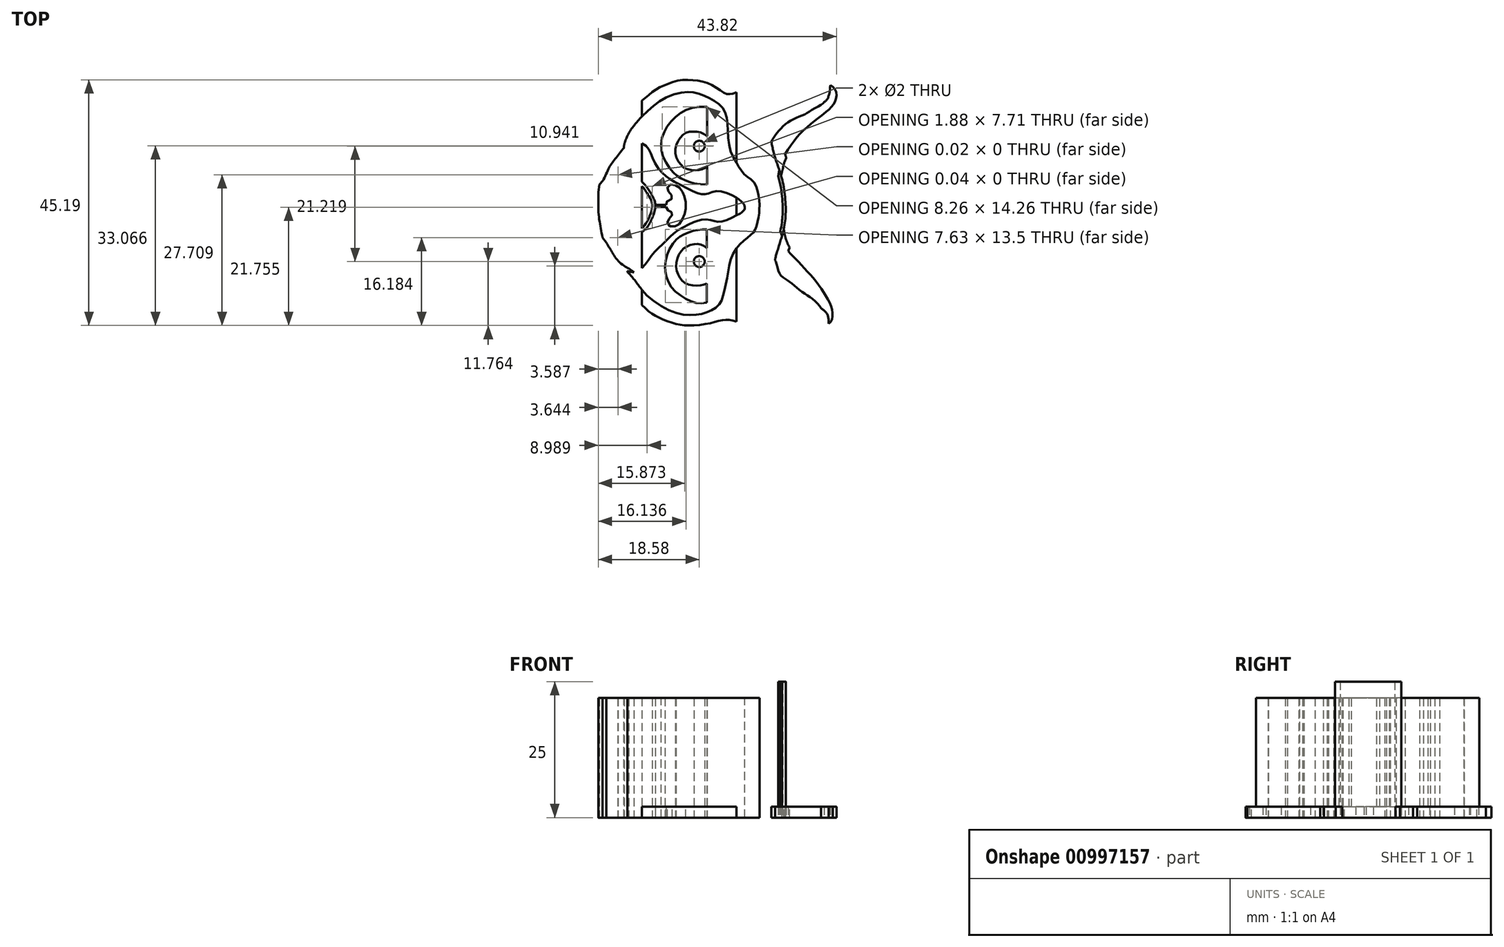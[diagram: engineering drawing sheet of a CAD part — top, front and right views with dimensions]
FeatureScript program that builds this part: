
annotation { "Feature Type Name" : "Feature", "Feature Type Description" : "" }
export const myFeature = defineFeature(function(context is Context, id is Id, definition is map)
    precondition{}
    {
        {
            var Q0;
            Q0=qCreatedBy(makeId("Top.planeOp"),FACE);
            var sketch = newSketch(context, id + "F0", { "sketchPlane" : qUnion([Q0])});
            skLineSegment(sketch, "E0", {"start": v(52.2, -25.32) * mm, "end": v(52.2, -39.58) * mm});
            skLineSegment(sketch, "E1", {"start": v(52.14, -47.83) * mm, "end": v(52.14, -61.33) * mm});
            skFitSpline(sketch, "E2", {"points": [v(52.2, -25.32) * mm, v(47.39, -26.41) * mm, v(44.48, -29.6) * mm, v(43.86, -33.55) * mm, v(45.93, -37.28) * mm, v(48, -38.74) * mm, v(50.09, -39.43) * mm, v(52.2, -39.58) * mm], "startDerivative": vector(-35.94, 2.58) * mm, "endDerivative": vector(39.25, -3.06) * mm});
            skFitSpline(sketch, "E3", {"points": [v(52.14, -61.33) * mm, v(50.12, -61.33) * mm, v(48.02, -60.44) * mm, v(45.82, -58.67) * mm, v(44.71, -56.52) * mm, v(44.48, -54.66) * mm, v(44.96, -52.24) * mm, v(46.4, -49.9) * mm, v(47.49, -49.02) * mm, v(49.12, -48.26) * mm, v(50.68, -47.93) * mm, v(52.14, -47.83) * mm], "startDerivative": vector(-24.82, -2.43) * mm, "endDerivative": vector(19.62, -0.27) * mm});
            skFitSpline(sketch, "E4", {"points": [v(52.14, -51.25) * mm, v(51.1, -50.64) * mm, v(49.91, -50.52) * mm, v(48.55, -50.96) * mm, v(47.44, -51.83) * mm, v(46.65, -53.43) * mm, v(46.57, -55.15) * mm, v(47.12, -56.58) * mm, v(48.17, -57.68) * mm, v(49.56, -58.15) * mm, v(51.14, -58.12) * mm, v(52.14, -57.83) * mm], "startDerivative": vector(-12, 8.58) * mm, "endDerivative": vector(12.04, 4.34) * mm});
            skFitSpline(sketch, "E5", {"points": [v(52.2, -30.7) * mm, v(51.23, -30.07) * mm, v(49.95, -29.86) * mm, v(48.84, -29.9) * mm, v(47.8, -30.42) * mm, v(46.94, -31.46) * mm, v(46.45, -32.77) * mm, v(46.45, -34.43) * mm, v(47.32, -35.85) * mm, v(48.18, -36.61) * mm, v(49.57, -36.96) * mm, v(50.74, -36.89) * mm, v(51.64, -36.61) * mm, v(52.2, -36.16) * mm], "startDerivative": vector(-12.11, 9.76) * mm, "endDerivative": vector(8.55, 8.45) * mm});
            skCircle(sketch, "E6", {"center": v(50.77, -53.76) * mm, "radius": 1 * mm});
            skCircle(sketch, "E7", {"center": v(50.77, -32.54) * mm, "radius": 1 * mm});
            skFitSpline(sketch, "E8", {"points": [v(35.01, -37.86) * mm, v(37.23, -37.99) * mm, v(39.56, -39.23) * mm, v(41.03, -40.95) * mm, v(41.77, -42.17) * mm, v(42.12, -43.51) * mm, v(41.57, -45.55) * mm, v(40.54, -47.31) * mm, v(39.33, -48.26) * mm, v(37.21, -49.17) * mm, v(34.82, -49.32) * mm], "startDerivative": vector(20.16, 2.55) * mm, "endDerivative": vector(-22.5, 0.89) * mm});
            skFitSpline(sketch, "E9.0", {"points": [v(34.94, -37.3) * mm, v(35.4, -37.25) * mm, v(36.1, -37.22) * mm, v(37.1, -37.36) * mm, v(37.86, -37.58) * mm, v(38.59, -37.9) * mm, v(39.28, -38.3) * mm, v(39.92, -38.78) * mm, v(40.48, -39.32) * mm, v(40.95, -39.88) * mm, v(41.35, -40.42) * mm, v(41.7, -40.92) * mm, v(41.99, -41.39) * mm, v(42.2, -41.78) * mm, v(42.36, -42.12) * mm, v(42.51, -42.48) * mm, v(42.63, -42.88) * mm, v(42.68, -43.32) * mm, v(42.68, -43.8) * mm, v(42.59, -44.38) * mm, v(42.37, -45.07) * mm, v(42.1, -45.74) * mm, v(41.8, -46.39) * mm, v(41.47, -47) * mm, v(41.16, -47.46) * mm, v(40.87, -47.8) * mm, v(40.57, -48.09) * mm, v(40.25, -48.34) * mm, v(39.92, -48.56) * mm, v(39.65, -48.72) * mm, v(39.38, -48.88) * mm, v(38.98, -49.1) * mm, v(38.43, -49.36) * mm, v(37.72, -49.63) * mm, v(36.97, -49.81) * mm, v(36.23, -49.89) * mm, v(35.5, -49.9) * mm, v(35.03, -49.89) * mm, v(34.8, -49.88) * mm]});
            skLineSegment(sketch, "E10", {"start": v(44.65, -43.32) * mm, "end": v(42.67, -43.32) * mm});
            skLineSegment(sketch, "E11", {"start": v(44.66, -43.71) * mm, "end": v(42.67, -43.71) * mm});
            skPoint(sketch, "E12.orphan", {"position": v(44.65, -43.51) * mm});
            skFitSpline(sketch, "E13.trimOffspring", {"points": [v(34.94, -37.3) * mm, v(35.4, -37.25) * mm, v(36.1, -37.22) * mm, v(37.1, -37.36) * mm, v(37.86, -37.58) * mm, v(38.59, -37.9) * mm, v(39.28, -38.3) * mm, v(39.92, -38.78) * mm, v(40.48, -39.32) * mm, v(40.95, -39.88) * mm, v(41.35, -40.42) * mm, v(41.7, -40.92) * mm, v(41.99, -41.39) * mm, v(42.2, -41.78) * mm, v(42.36, -42.12) * mm, v(42.51, -42.48) * mm, v(42.63, -42.88) * mm, v(42.68, -43.32) * mm, v(42.68, -43.8) * mm, v(42.59, -44.38) * mm, v(42.37, -45.07) * mm, v(42.1, -45.74) * mm, v(41.8, -46.39) * mm, v(41.47, -47) * mm, v(41.16, -47.46) * mm, v(40.87, -47.8) * mm, v(40.57, -48.09) * mm, v(40.25, -48.34) * mm, v(39.92, -48.56) * mm, v(39.65, -48.72) * mm, v(39.38, -48.88) * mm, v(38.98, -49.1) * mm, v(38.43, -49.36) * mm, v(37.72, -49.63) * mm, v(36.97, -49.81) * mm, v(36.23, -49.89) * mm, v(35.5, -49.9) * mm, v(35.03, -49.89) * mm, v(34.8, -49.88) * mm]});
            skPoint(sketch, "E14.third.point", {"position": v(34.82, -37.86) * mm});
            skArc(sketch, "E15", {"start": v(34.77, -49.88) * mm, "mid": v(34.78, -49.88) * mm, "end": v(34.8, -49.88) * mm});
            skPoint(sketch, "E15.third.point", {"position": v(34.77, -49.88) * mm});
            skFitSpline(sketch, "E16", {"points": [v(44.66, -43.71) * mm, v(44.87, -44.24) * mm, v(45.29, -44.53) * mm, v(45.7, -44.7) * mm, v(45.82, -45) * mm, v(45.57, -45.5) * mm, v(45.12, -46) * mm, v(44.92, -46.48) * mm, v(45.12, -47.1) * mm, v(45.82, -47.32) * mm, v(46.63, -47.2) * mm, v(47.22, -46.71) * mm, v(47.77, -45.74) * mm, v(48.18, -44.68) * mm, v(48.29, -43.71) * mm, v(48.18, -42.21) * mm, v(47.95, -41.54) * mm, v(47.59, -40.82) * mm, v(47.03, -40.07) * mm, v(46.38, -39.69) * mm, v(45.59, -39.58) * mm, v(45, -39.89) * mm, v(44.92, -40.48) * mm, v(45.2, -40.95) * mm, v(45.66, -41.56) * mm, v(45.78, -42.16) * mm, v(45.14, -42.44) * mm, v(44.66, -42.96) * mm, v(44.65, -43.32) * mm], "startDerivative": vector(-1.35, -20.13) * mm, "endDerivative": vector(4.82, -19.1) * mm});
            skFitSpline(sketch, "E17", {"points": [v(61.85, -43.78) * mm, v(61.66, -45.64) * mm, v(61.1, -47.77) * mm, v(60.36, -48.77) * mm, v(58.46, -50.33) * mm, v(56.64, -53.16) * mm, v(55.93, -56.55) * mm, v(55.22, -59.79) * mm, v(54.44, -61.65) * mm, v(52.73, -62.88) * mm, v(50.2, -63.55) * mm, v(46.29, -63.14) * mm, v(40.9, -59.71) * mm, v(38.44, -56.62) * mm, v(37.55, -55.56) * mm, v(39.03, -55.7) * mm, v(40.9, -54.17) * mm, v(42.5, -52.08) * mm, v(44.65, -49.92) * mm, v(46.66, -48.14) * mm, v(49.64, -46.57) * mm, v(51.43, -46.02) * mm, v(53.4, -46.24) * mm, v(54.63, -46.46) * mm, v(57.2, -45.46) * mm, v(58.6, -44.68) * mm, v(59.13, -44.04) * mm, v(59.13, -43.6) * mm, v(58.83, -43) * mm, v(57.83, -42.15) * mm, v(56.49, -41.44) * mm, v(54.51, -40.8) * mm, v(53.17, -41) * mm, v(52.36, -41.29) * mm, v(51.57, -41.36) * mm, v(50.57, -41.21) * mm, v(48.9, -40.47) * mm, v(46.1, -39.02) * mm, v(44.8, -38.16) * mm, v(43.54, -37) * mm, v(42.3, -34.96) * mm, v(41.71, -33.55) * mm, v(41.04, -32.54) * mm, v(39.7, -31.8) * mm, v(38.06, -31.8) * mm, v(36.95, -32.8) * mm, v(37.17, -31.58) * mm, v(38.66, -28.86) * mm, v(41.53, -25.84) * mm, v(44.43, -23.69) * mm, v(48.11, -22.57) * mm, v(50.23, -22.76) * mm, v(52.24, -23.5) * mm, v(53.92, -24.47) * mm, v(55.26, -25.77) * mm, v(55.85, -27.6) * mm, v(56.08, -30.53) * mm, v(56.56, -33.59) * mm, v(57.72, -35.74) * mm, v(59.06, -37.72) * mm, v(60.73, -39.06) * mm, v(61.62, -41.25) * mm, v(61.85, -43.78) * mm]});
            skFitSpline(sketch, "E18", {"points": [v(64.7, -53.55) * mm, v(65.46, -55.81) * mm, v(66.99, -57.18) * mm, v(69.43, -59.13) * mm, v(72.07, -61.03) * mm, v(73.3, -62.63) * mm, v(72.88, -62.6) * mm, v(69.9, -62.87) * mm, v(66.9, -62.97) * mm, v(64.85, -61.66) * mm, v(63.46, -59.2) * mm, v(63.04, -56.95) * mm, v(63.64, -55.13) * mm, v(64.7, -53.55) * mm]});
            skFitSpline(sketch, "E19", {"points": [v(64.02, -31.7) * mm, v(64.56, -34.1) * mm, v(65.35, -36.47) * mm, v(66.19, -39.41) * mm, v(66.66, -43.47) * mm, v(66.5, -46.78) * mm, v(65.82, -49.6) * mm, v(64.77, -53.12) * mm, v(64.7, -53.55) * mm], "startDerivative": vector(3.95, -20.11) * mm, "endDerivative": vector(-0.5, -6.13) * mm});
            skFitSpline(sketch, "E20.0", {"points": [v(63.47, -31.8) * mm, v(63.55, -32.22) * mm, v(63.68, -32.86) * mm, v(63.87, -33.7) * mm, v(64.04, -34.34) * mm, v(64.23, -34.97) * mm, v(64.51, -35.78) * mm, v(64.88, -36.8) * mm, v(65.3, -38.08) * mm, v(65.65, -39.47) * mm, v(65.91, -41.04) * mm, v(66.05, -42.4) * mm, v(66.1, -43.48) * mm, v(66.12, -44.26) * mm, v(66.1, -45) * mm, v(66.06, -45.72) * mm, v(66, -46.4) * mm, v(65.87, -47.23) * mm, v(65.7, -48.02) * mm, v(65.47, -48.8) * mm, v(65.32, -49.3) * mm, v(65.16, -49.83) * mm, v(64.94, -50.55) * mm, v(64.68, -51.41) * mm, v(64.44, -52.2) * mm, v(64.29, -52.73) * mm, v(64.2, -53.05) * mm, v(64.16, -53.3) * mm, v(64.15, -53.44) * mm, v(64.14, -53.5) * mm]});
            skFitSpline(sketch, "E20.1", {"points": [v(63.47, -31.8) * mm, v(63.55, -32.22) * mm, v(63.68, -32.86) * mm, v(63.87, -33.7) * mm, v(64.04, -34.34) * mm, v(64.23, -34.97) * mm, v(64.51, -35.78) * mm, v(64.88, -36.8) * mm, v(65.3, -38.08) * mm, v(65.65, -39.47) * mm, v(65.91, -41.04) * mm, v(66.05, -42.4) * mm, v(66.1, -43.48) * mm, v(66.12, -44.26) * mm, v(66.1, -45) * mm, v(66.06, -45.72) * mm, v(66, -46.4) * mm, v(65.87, -47.23) * mm, v(65.7, -48.02) * mm, v(65.47, -48.8) * mm, v(65.32, -49.3) * mm, v(65.16, -49.83) * mm, v(64.94, -50.55) * mm, v(64.68, -51.41) * mm, v(64.44, -52.2) * mm, v(64.29, -52.73) * mm, v(64.2, -53.05) * mm, v(64.16, -53.3) * mm, v(64.15, -53.44) * mm, v(64.14, -53.5) * mm]});
            skFitSpline(sketch, "E20.2", {"points": [v(63.47, -31.8) * mm, v(63.55, -32.22) * mm, v(63.68, -32.86) * mm, v(63.87, -33.7) * mm, v(64.04, -34.34) * mm, v(64.23, -34.97) * mm, v(64.51, -35.78) * mm, v(64.88, -36.8) * mm, v(65.3, -38.08) * mm, v(65.65, -39.47) * mm, v(65.91, -41.04) * mm, v(66.05, -42.4) * mm, v(66.1, -43.48) * mm, v(66.12, -44.26) * mm, v(66.1, -45) * mm, v(66.06, -45.72) * mm, v(66, -46.4) * mm, v(65.87, -47.23) * mm, v(65.7, -48.02) * mm, v(65.47, -48.8) * mm, v(65.32, -49.3) * mm, v(65.16, -49.83) * mm, v(64.94, -50.55) * mm, v(64.68, -51.41) * mm, v(64.44, -52.2) * mm, v(64.29, -52.73) * mm, v(64.2, -53.05) * mm, v(64.16, -53.3) * mm, v(64.15, -53.44) * mm, v(64.14, -53.5) * mm]});
            skLineSegment(sketch, "E21", {"start": v(64.14, -53.47) * mm, "end": v(64.06, -54.29) * mm});
            skLineSegment(sketch, "E22", {"start": v(65.48, -36.87) * mm, "end": v(65.28, -38.1) * mm});
            skLineSegment(sketch, "E23", {"start": v(65.98, -49.06) * mm, "end": v(65.66, -48.12) * mm});
            skFitSpline(sketch, "E24", {"points": [v(36.95, -32.8) * mm, v(35.31, -34.84) * mm, v(34.2, -36.44) * mm, v(33.01, -38.91) * mm], "startDerivative": vector(-5.17, -6.03) * mm, "endDerivative": vector(-3.98, -7.08) * mm});
            skFitSpline(sketch, "E25", {"points": [v(37.55, -55.56) * mm, v(35.43, -53.97) * mm, v(34.08, -52.05) * mm, v(33.19, -50.54) * mm], "startDerivative": vector(-6.96, 3.5) * mm, "endDerivative": vector(-3.36, 5.63) * mm});
            skFitSpline(sketch, "E26.0", {"points": [v(36.52, -32.44) * mm, v(36.3, -32.7) * mm, v(35.88, -33.21) * mm, v(35.38, -33.84) * mm, v(35.01, -34.32) * mm, v(34.66, -34.76) * mm, v(34.25, -35.3) * mm, v(33.86, -35.9) * mm, v(33.56, -36.45) * mm, v(33.3, -37.03) * mm, v(32.96, -37.78) * mm, v(32.68, -38.36) * mm, v(32.52, -38.64) * mm]});
            skLineSegment(sketch, "E27", {"start": v(36.5, -32.46) * mm, "end": v(37.1, -31.79) * mm});
            skFitSpline(sketch, "E28.0", {"points": [v(37.8, -55.06) * mm, v(37.53, -54.92) * mm, v(37.03, -54.63) * mm, v(36.36, -54.13) * mm, v(35.78, -53.55) * mm, v(35.27, -52.89) * mm, v(34.88, -52.3) * mm, v(34.6, -51.85) * mm, v(34.35, -51.42) * mm, v(34.06, -50.92) * mm, v(33.8, -50.49) * mm, v(33.67, -50.25) * mm]});
            skLineSegment(sketch, "E29", {"start": v(37.77, -55.04) * mm, "end": v(38.78, -55.7) * mm});
            skFitSpline(sketch, "E30", {"points": [v(64.02, -31.7) * mm, v(64.72, -30.54) * mm, v(66.12, -28.96) * mm, v(67.85, -27.68) * mm, v(69.93, -26.78) * mm, v(71.39, -25.93) * mm, v(73.56, -24.66) * mm, v(73.77, -24.27) * mm, v(73.06, -24.09) * mm, v(69.77, -23.64) * mm, v(67.9, -23.32) * mm, v(65.7, -23.9) * mm, v(63.89, -26.15) * mm, v(63.5, -29.37) * mm, v(63.47, -31.8) * mm], "startDerivative": vector(10.48, 19) * mm, "endDerivative": vector(-0.33, -29.39) * mm});
            skFitSpline(sketch, "E31", {"points": [v(73.77, -24.4) * mm, v(74.29, -23.95) * mm, v(74.64, -23.03) * mm, v(74.79, -22.37) * mm, v(74.87, -21.33) * mm], "startDerivative": vector(2.47, 1.63) * mm, "endDerivative": vector(0.2, 4.02) * mm});
            skFitSpline(sketch, "E32.0", {"points": [v(73.46, -23.93) * mm, v(73.51, -23.9) * mm, v(73.6, -23.83) * mm, v(73.72, -23.75) * mm, v(73.8, -23.68) * mm, v(73.85, -23.6) * mm, v(73.92, -23.46) * mm, v(73.99, -23.28) * mm, v(74.05, -23.08) * mm, v(74.1, -22.87) * mm, v(74.16, -22.69) * mm, v(74.2, -22.53) * mm, v(74.22, -22.38) * mm, v(74.25, -22.16) * mm, v(74.28, -21.8) * mm, v(74.3, -21.47) * mm, v(74.3, -21.3) * mm]});
            skFitSpline(sketch, "E33", {"points": [v(73.46, -23.93) * mm, v(73.22, -24.1) * mm], "startDerivative": vector(-0.24, -0.17) * mm, "endDerivative": vector(-0.24, -0.17) * mm});
            skFitSpline(sketch, "E34", {"points": [v(74.87, -21.33) * mm, v(75.7, -21.98) * mm, v(76, -23.09) * mm, v(75.75, -24.28) * mm, v(75.22, -25.17) * mm, v(74.25, -26.11) * mm, v(73.06, -27.06) * mm, v(71.75, -28.06) * mm, v(69.75, -29.82) * mm, v(68.14, -31.64) * mm, v(66.4, -34.24) * mm, v(65.69, -36.05) * mm, v(65.48, -36.87) * mm], "startDerivative": vector(13.76, -8.17) * mm, "endDerivative": vector(-6.9, -11.6) * mm});
            skFitSpline(sketch, "E35", {"points": [v(65.98, -49.06) * mm, v(66.37, -50.34) * mm, v(67.36, -52.1) * mm, v(68.55, -53.31) * mm, v(70.18, -55.08) * mm, v(71.83, -56.88) * mm, v(73.43, -59.12) * mm, v(74.6, -60.97) * mm, v(75.2, -62.64) * mm, v(75.26, -64.05) * mm, v(74.78, -65.03) * mm, v(73.96, -65.46) * mm, v(71.52, -65.7) * mm, v(67.5, -65.93) * mm, v(63.56, -65.9) * mm, v(60.74, -65.42) * mm, v(58.27, -64.99) * mm, v(56.45, -64.49) * mm, v(54.83, -64.58) * mm, v(52.35, -65.17) * mm, v(48.53, -65.52) * mm, v(46.25, -65.14) * mm, v(43.53, -64.14) * mm, v(41.65, -63.05) * mm, v(39.68, -61.17) * mm, v(37.83, -59.23) * mm, v(35.86, -56.76) * mm, v(34.48, -54.35) * mm, v(33.58, -52.4) * mm, v(33.19, -50.54) * mm], "startDerivative": vector(11.73, -46.26) * mm, "endDerivative": vector(-8.89, 60.13) * mm});
            skFitSpline(sketch, "E36", {"points": [v(33.19, -50.54) * mm, v(32.82, -48.55) * mm, v(32.48, -46.7) * mm, v(32.22, -44.64) * mm, v(32.2, -42.78) * mm, v(32.24, -40.98) * mm, v(32.52, -38.64) * mm], "startDerivative": vector(-2.24, 11.99) * mm, "endDerivative": vector(1.9, 13.38) * mm});
            skFitSpline(sketch, "E37", {"points": [v(32.52, -38.64) * mm, v(32.9, -36.5) * mm, v(33.85, -33.68) * mm, v(34.7, -31.52) * mm, v(35.57, -29.74) * mm, v(36.76, -27.8) * mm, v(38.23, -26.06) * mm, v(39.6, -24.73) * mm, v(41.03, -23.5) * mm, v(42.75, -22.15) * mm, v(44.69, -21.2) * mm, v(47, -20.45) * mm, v(49.66, -20.4) * mm, v(52.16, -20.9) * mm, v(54.42, -22.11) * mm, v(55.82, -22.93) * mm, v(56.67, -22.93) * mm, v(58.14, -22.5) * mm, v(61.25, -21.65) * mm, v(64.77, -20.5) * mm, v(68.4, -20.28) * mm, v(71.88, -20.7) * mm, v(74.3, -21.3) * mm, v(74.87, -21.33) * mm], "startDerivative": vector(6.5, 48.11) * mm, "endDerivative": vector(21.47, 0.89) * mm});
            skFitSpline(sketch, "E38", {"points": [v(72.88, -62.6) * mm, v(73.77, -63.33) * mm, v(74.07, -63.96) * mm, v(74.2, -64.86) * mm, v(74.2, -65.39) * mm], "startDerivative": vector(3.43, -2.41) * mm, "endDerivative": vector(0, -2.36) * mm});
            skFitSpline(sketch, "E39", {"points": [v(73.17, -62.32) * mm, v(73.96, -62.97) * mm, v(74.44, -63.8) * mm, v(74.59, -64.7) * mm, v(74.6, -65.2) * mm], "startDerivative": vector(3.03, -2.2) * mm, "endDerivative": vector(0, -2.32) * mm});
            skFitSpline(sketch, "E40.0", {"points": [v(66.52, -48.92) * mm, v(66.58, -49.16) * mm, v(66.67, -49.5) * mm, v(66.83, -49.99) * mm, v(67, -50.38) * mm, v(67.2, -50.8) * mm, v(67.42, -51.2) * mm, v(67.67, -51.59) * mm, v(67.93, -51.9) * mm, v(68.2, -52.2) * mm, v(68.5, -52.49) * mm, v(68.83, -52.8) * mm, v(69.31, -53.3) * mm, v(69.8, -53.83) * mm, v(70.3, -54.38) * mm, v(70.65, -54.77) * mm, v(71.02, -55.16) * mm, v(71.51, -55.67) * mm, v(72.01, -56.2) * mm, v(72.5, -56.81) * mm, v(72.85, -57.29) * mm, v(73.2, -57.77) * mm, v(73.52, -58.25) * mm, v(73.84, -58.72) * mm, v(74.24, -59.31) * mm, v(74.63, -59.89) * mm, v(74.99, -60.48) * mm, v(75.3, -61.1) * mm, v(75.54, -61.72) * mm, v(75.71, -62.35) * mm, v(75.8, -62.8) * mm, v(75.87, -63.28) * mm, v(75.87, -63.76) * mm, v(75.8, -64.24) * mm, v(75.66, -64.7) * mm, v(75.44, -65.11) * mm, v(75.16, -65.47) * mm, v(74.8, -65.75) * mm, v(74.39, -65.93) * mm, v(73.95, -66.04) * mm, v(73.46, -66.11) * mm, v(72.91, -66.17) * mm, v(72.33, -66.2) * mm, v(71.7, -66.24) * mm, v(70.85, -66.3) * mm, v(69.72, -66.36) * mm, v(68.3, -66.45) * mm, v(66.86, -66.52) * mm, v(65.43, -66.55) * mm, v(64.28, -66.52) * mm, v(63.4, -66.45) * mm, v(62.78, -66.36) * mm, v(62.18, -66.26) * mm, v(61.62, -66.16) * mm, v(61.06, -66.05) * mm, v(60.35, -65.92) * mm, v(59.61, -65.82) * mm, v(58.88, -65.7) * mm, v(58.33, -65.59) * mm, v(57.8, -65.44) * mm, v(57.17, -65.24) * mm, v(56.62, -65.07) * mm, v(56.15, -65) * mm, v(55.79, -65) * mm, v(55.4, -65.04) * mm, v(54.85, -65.14) * mm, v(54.08, -65.34) * mm, v(53.16, -65.58) * mm, v(52.3, -65.76) * mm, v(51.38, -65.91) * mm, v(50.16, -66.05) * mm, v(49, -66.1) * mm, v(48.17, -66.07) * mm, v(47.42, -66) * mm, v(46.73, -65.86) * mm, v(46.03, -65.66) * mm, v(45.28, -65.43) * mm, v(44.5, -65.15) * mm, v(43.74, -64.85) * mm, v(43.03, -64.54) * mm, v(42.24, -64.15) * mm, v(41.36, -63.56) * mm, v(40.48, -62.79) * mm, v(39.78, -62.08) * mm, v(39.25, -61.53) * mm, v(38.72, -61) * mm, v(38.08, -60.33) * mm, v(37.3, -59.48) * mm, v(36.48, -58.54) * mm, v(35.83, -57.7) * mm, v(35.34, -57) * mm, v(34.9, -56.3) * mm, v(34.52, -55.6) * mm, v(34.17, -54.95) * mm, v(33.83, -54.32) * mm, v(33.5, -53.7) * mm, v(33.22, -53.07) * mm, v(33.03, -52.57) * mm, v(32.9, -52.07) * mm, v(32.75, -51.41) * mm, v(32.68, -50.93) * mm, v(32.63, -50.62) * mm]});
            skFitSpline(sketch, "E41", {"points": [v(66.52, -48.92) * mm, v(66.33, -47.72) * mm], "startDerivative": vector(-0.2, 1.2) * mm, "endDerivative": vector(-0.2, 1.2) * mm});
            skFitSpline(sketch, "E42.0", {"points": [v(32.64, -50.64) * mm, v(32.54, -50.14) * mm, v(32.4, -49.39) * mm, v(32.22, -48.42) * mm, v(32.1, -47.71) * mm, v(31.97, -47) * mm, v(31.84, -46.24) * mm, v(31.73, -45.46) * mm, v(31.65, -44.67) * mm, v(31.63, -43.9) * mm, v(31.63, -43.16) * mm, v(31.64, -42.48) * mm, v(31.64, -41.78) * mm, v(31.67, -41.03) * mm, v(31.74, -40.23) * mm, v(31.85, -39.4) * mm, v(31.93, -38.84) * mm, v(31.97, -38.56) * mm]});
            skFitSpline(sketch, "E43.0", {"points": [v(31.97, -38.56) * mm, v(32, -38.31) * mm, v(32.07, -37.8) * mm, v(32.19, -37.14) * mm, v(32.3, -36.57) * mm, v(32.46, -35.98) * mm, v(32.7, -35.21) * mm, v(33.02, -34.3) * mm, v(33.35, -33.42) * mm, v(33.65, -32.6) * mm, v(33.94, -31.85) * mm, v(34.25, -31.12) * mm, v(34.58, -30.42) * mm, v(34.93, -29.73) * mm, v(35.44, -28.8) * mm, v(36.03, -27.82) * mm, v(36.73, -26.9) * mm, v(37.28, -26.25) * mm, v(37.84, -25.65) * mm, v(38.39, -25.1) * mm, v(38.93, -24.58) * mm, v(39.49, -24.08) * mm, v(40.05, -23.6) * mm, v(40.52, -23.2) * mm, v(40.91, -22.87) * mm, v(41.32, -22.52) * mm, v(41.75, -22.16) * mm, v(42.21, -21.83) * mm, v(42.7, -21.51) * mm, v(43.31, -21.19) * mm, v(44.06, -20.86) * mm, v(44.81, -20.55) * mm, v(45.62, -20.24) * mm, v(46.34, -20.02) * mm, v(46.95, -19.89) * mm, v(47.58, -19.8) * mm, v(48.36, -19.76) * mm, v(49.29, -19.8) * mm, v(50.19, -19.87) * mm, v(51.09, -20) * mm, v(51.98, -20.22) * mm, v(52.86, -20.56) * mm, v(53.7, -21) * mm, v(54.33, -21.38) * mm, v(54.8, -21.7) * mm, v(55.13, -21.91) * mm, v(55.42, -22.1) * mm, v(55.68, -22.26) * mm, v(55.9, -22.37) * mm, v(56.06, -22.41) * mm, v(56.2, -22.43) * mm, v(56.35, -22.42) * mm, v(56.55, -22.38) * mm, v(56.88, -22.3) * mm, v(57.29, -22.16) * mm, v(57.77, -22.01) * mm, v(58.31, -21.86) * mm, v(59.05, -21.67) * mm, v(60.01, -21.43) * mm, v(60.82, -21.2) * mm, v(61.46, -20.99) * mm, v(62.1, -20.76) * mm, v(62.93, -20.45) * mm, v(63.77, -20.17) * mm, v(64.47, -19.98) * mm, v(65.19, -19.83) * mm, v(66.09, -19.72) * mm, v(67.16, -19.68) * mm, v(68.22, -19.7) * mm, v(69.26, -19.76) * mm, v(70.29, -19.86) * mm, v(71.14, -19.98) * mm, v(71.82, -20.11) * mm, v(72.33, -20.23) * mm, v(72.82, -20.35) * mm, v(73.28, -20.47) * mm, v(73.7, -20.58) * mm, v(74.07, -20.68) * mm, v(74.37, -20.74) * mm, v(74.56, -20.77) * mm, v(74.7, -20.77) * mm, v(74.79, -20.77) * mm, v(74.84, -20.77) * mm]});
            skFitSpline(sketch, "E44.0", {"points": [v(75.15, -20.85) * mm, v(75.3, -20.93) * mm, v(75.53, -21.07) * mm, v(75.85, -21.32) * mm, v(76.08, -21.55) * mm, v(76.28, -21.84) * mm, v(76.42, -22.15) * mm, v(76.51, -22.48) * mm, v(76.56, -22.8) * mm, v(76.57, -23.14) * mm, v(76.54, -23.58) * mm, v(76.45, -23.98) * mm, v(76.32, -24.36) * mm, v(76.18, -24.7) * mm, v(75.96, -25.11) * mm, v(75.63, -25.57) * mm, v(75.22, -26) * mm, v(74.77, -26.4) * mm, v(74.31, -26.79) * mm, v(73.85, -27.16) * mm, v(73.37, -27.53) * mm, v(72.91, -27.87) * mm, v(72.44, -28.22) * mm, v(71.92, -28.63) * mm, v(71.34, -29.12) * mm, v(70.75, -29.64) * mm, v(70.18, -30.17) * mm, v(69.68, -30.68) * mm, v(69.22, -31.2) * mm, v(68.77, -31.74) * mm, v(68.3, -32.36) * mm, v(67.8, -33.04) * mm, v(67.34, -33.74) * mm, v(66.93, -34.44) * mm, v(66.6, -35.09) * mm, v(66.4, -35.57) * mm, v(66.3, -35.91) * mm, v(66.25, -36.1) * mm, v(66.22, -36.23) * mm, v(66.2, -36.38) * mm, v(66.17, -36.57) * mm, v(66.11, -36.85) * mm, v(66.02, -37.05) * mm, v(65.96, -37.16) * mm]});
            skFitSpline(sketch, "E45", {"points": [v(75.15, -20.85) * mm, v(74.84, -20.77) * mm], "startDerivative": vector(-0.3, 0.08) * mm, "endDerivative": vector(-0.3, 0.08) * mm});
            skFitSpline(sketch, "E46", {"points": [v(65.96, -37.16) * mm, v(65.83, -37.99) * mm], "startDerivative": vector(-0.13, -0.83) * mm, "endDerivative": vector(-0.13, -0.83) * mm});
            skLineSegment(sketch, "E47", {"start": v(33.67, -50.25) * mm, "end": v(32.96, -49.33) * mm});
            skLineSegment(sketch, "E48", {"start": v(33.01, -38.91) * mm, "end": v(32.4, -39.59) * mm});
            skFitSpline(sketch, "E49", {"points": [v(74.3, -21.3) * mm, v(74.3, -21.3) * mm, v(74.34, -21) * mm], "startDerivative": vector(0, 0.16) * mm, "endDerivative": vector(0.04, 0.41) * mm});
            skFitSpline(sketch, "E50.trimOffspring", {"points": [v(64.02, -31.7) * mm, v(64.72, -30.54) * mm, v(66.12, -28.96) * mm, v(67.85, -27.68) * mm, v(69.93, -26.78) * mm, v(71.39, -25.93) * mm, v(73.56, -24.66) * mm, v(73.77, -24.27) * mm, v(73.06, -24.09) * mm, v(69.77, -23.64) * mm, v(67.9, -23.32) * mm, v(65.7, -23.9) * mm, v(63.89, -26.15) * mm, v(63.5, -29.37) * mm, v(63.47, -31.8) * mm], "startDerivative": vector(10.48, 19) * mm, "endDerivative": vector(-0.33, -29.39) * mm});
            skArc(sketch, "E51", {"start": v(35.85, -37.25) * mm, "mid": v(35.55, -37.53) * mm, "end": v(35.85, -37.81) * mm});
            skPoint(sketch, "E51.first.point", {"position": v(35.82, -37.25) * mm});
            skPoint(sketch, "E51.second.point", {"position": v(35.85, -37.81) * mm});
            skPoint(sketch, "E51.third.point", {"position": v(35.56, -37.5) * mm});
            skArc(sketch, "E52", {"start": v(35.8, -49.34) * mm, "mid": v(35.5, -49.63) * mm, "end": v(35.82, -49.9) * mm});
            skPoint(sketch, "E52.first.point", {"position": v(35.8, -49.34) * mm});
            skPoint(sketch, "E52.second.point", {"position": v(35.75, -49.9) * mm});
            skPoint(sketch, "E52.third.point", {"position": v(35.82, -49.9) * mm});
            skFitSpline(sketch, "E53.0", {"points": [v(76.14, -19.18) * mm, v(76.22, -19.22) * mm, v(76.4, -19.33) * mm, v(76.73, -19.55) * mm, v(77.14, -19.86) * mm, v(77.5, -20.23) * mm, v(77.8, -20.61) * mm, v(77.97, -20.9) * mm, v(78.12, -21.2) * mm, v(78.28, -21.58) * mm, v(78.41, -22.06) * mm, v(78.48, -22.53) * mm, v(78.5, -22.9) * mm, v(78.51, -23.28) * mm, v(78.47, -23.72) * mm, v(78.39, -24.2) * mm, v(78.27, -24.64) * mm, v(78.13, -25.04) * mm, v(77.99, -25.4) * mm, v(77.8, -25.77) * mm, v(77.6, -26.14) * mm, v(77.36, -26.49) * mm, v(77.1, -26.82) * mm, v(76.83, -27.12) * mm, v(76.48, -27.48) * mm, v(76.13, -27.8) * mm, v(75.8, -28.08) * mm, v(75.46, -28.35) * mm, v(75.13, -28.62) * mm, v(74.8, -28.88) * mm, v(74.54, -29.07) * mm, v(74.3, -29.25) * mm, v(74, -29.48) * mm, v(73.62, -29.76) * mm, v(73.15, -30.14) * mm, v(72.6, -30.59) * mm, v(72.06, -31.08) * mm, v(71.53, -31.57) * mm, v(71.1, -32.01) * mm, v(70.7, -32.46) * mm, v(70.3, -32.94) * mm, v(69.85, -33.51) * mm, v(69.4, -34.14) * mm, v(68.98, -34.78) * mm, v(68.68, -35.28) * mm, v(68.5, -35.64) * mm, v(68.37, -35.89) * mm, v(68.28, -36.11) * mm, v(68.2, -36.3) * mm, v(68.17, -36.42) * mm, v(68.15, -36.5) * mm, v(68.14, -36.53) * mm, v(68.14, -36.54) * mm, v(68.13, -36.57) * mm, v(68.12, -36.63) * mm, v(68.1, -36.74) * mm, v(68.08, -36.91) * mm, v(68.03, -37.14) * mm, v(67.93, -37.53) * mm, v(67.78, -37.9) * mm, v(67.63, -38.15) * mm]});
            skFitSpline(sketch, "E54.0", {"points": [v(65.92, -31.32) * mm, v(65.96, -31.53) * mm, v(66.04, -31.95) * mm, v(66.17, -32.54) * mm, v(66.28, -33.01) * mm, v(66.37, -33.38) * mm, v(66.44, -33.65) * mm, v(66.52, -33.92) * mm, v(66.64, -34.28) * mm, v(66.87, -34.95) * mm, v(67.16, -35.77) * mm, v(67.46, -36.68) * mm, v(67.68, -37.4) * mm, v(67.9, -38.16) * mm, v(68.08, -38.97) * mm, v(68.25, -39.84) * mm, v(68.42, -41) * mm, v(68.57, -42.51) * mm, v(68.64, -44.28) * mm, v(68.58, -45.66) * mm, v(68.48, -46.7) * mm, v(68.37, -47.45) * mm, v(68.22, -48.18) * mm, v(68.04, -48.89) * mm, v(67.84, -49.62) * mm, v(67.6, -50.42) * mm, v(67.33, -51.29) * mm, v(67.11, -52) * mm, v(66.95, -52.53) * mm, v(66.84, -52.9) * mm, v(66.75, -53.2) * mm, v(66.68, -53.45) * mm, v(66.65, -53.59) * mm, v(66.64, -53.64) * mm, v(66.64, -53.65) * mm, v(66.64, -53.66) * mm, v(66.64, -53.66) * mm, v(66.63, -53.68) * mm, v(66.63, -53.7) * mm]});
            skFitSpline(sketch, "E55.0", {"points": [v(68.4, -48.44) * mm, v(68.46, -48.68) * mm, v(68.54, -48.97) * mm, v(68.64, -49.27) * mm, v(68.7, -49.44) * mm, v(68.79, -49.63) * mm, v(68.91, -49.9) * mm, v(69.06, -50.15) * mm, v(69.17, -50.34) * mm, v(69.26, -50.46) * mm, v(69.33, -50.55) * mm, v(69.42, -50.67) * mm, v(69.57, -50.82) * mm, v(69.83, -51.07) * mm, v(70.12, -51.35) * mm, v(70.4, -51.63) * mm, v(70.6, -51.84) * mm, v(70.8, -52.05) * mm, v(71.06, -52.33) * mm, v(71.37, -52.68) * mm, v(71.67, -53.01) * mm, v(71.9, -53.26) * mm, v(72.12, -53.5) * mm, v(72.41, -53.8) * mm, v(72.8, -54.2) * mm, v(73.2, -54.63) * mm, v(73.54, -55.02) * mm, v(73.83, -55.37) * mm, v(74.1, -55.72) * mm, v(74.43, -56.16) * mm, v(74.8, -56.67) * mm, v(75.13, -57.17) * mm, v(75.39, -57.55) * mm, v(75.59, -57.84) * mm, v(75.79, -58.14) * mm, v(76.05, -58.52) * mm, v(76.37, -59) * mm, v(76.68, -59.53) * mm, v(76.98, -60.12) * mm, v(77.23, -60.71) * mm, v(77.44, -61.3) * mm, v(77.57, -61.8) * mm, v(77.66, -62.18) * mm, v(77.74, -62.59) * mm, v(77.8, -63.13) * mm, v(77.82, -63.74) * mm, v(77.77, -64.26) * mm, v(77.7, -64.67) * mm, v(77.58, -65.07) * mm, v(77.4, -65.57) * mm, v(77.15, -66.05) * mm, v(76.82, -66.5) * mm, v(76.53, -66.83) * mm, v(76.18, -67.14) * mm, v(75.79, -67.4) * mm, v(75.39, -67.61) * mm, v(75, -67.76) * mm, v(74.65, -67.87) * mm, v(74.2, -67.96) * mm, v(73.68, -68.04) * mm, v(73.07, -68.1) * mm, v(72.44, -68.14) * mm, v(71.92, -68.17) * mm, v(71.5, -68.2) * mm, v(70.86, -68.24) * mm, v(69.84, -68.3) * mm, v(68.4, -68.39) * mm, v(66.94, -68.46) * mm, v(65.69, -68.49) * mm, v(64.69, -68.47) * mm, v(64.06, -68.44) * mm, v(63.57, -68.4) * mm, v(63.07, -68.36) * mm, v(62.49, -68.28) * mm, v(61.84, -68.17) * mm, v(61.25, -68.06) * mm, v(60.8, -67.97) * mm, v(60.45, -67.91) * mm, v(60.13, -67.86) * mm, v(59.7, -67.79) * mm, v(59.13, -67.7) * mm, v(58.53, -67.6) * mm, v(58.06, -67.5) * mm, v(57.74, -67.43) * mm, v(57.52, -67.38) * mm, v(57.26, -67.3) * mm, v(56.99, -67.22) * mm, v(56.67, -67.12) * mm, v(56.34, -67.02) * mm, v(56.16, -66.97) * mm, v(56.1, -66.96) * mm, v(56.06, -66.95) * mm, v(56.01, -66.95) * mm, v(55.95, -66.95) * mm, v(55.85, -66.95) * mm, v(55.68, -66.96) * mm, v(55.4, -67.01) * mm, v(55.02, -67.1) * mm, v(54.56, -67.22) * mm, v(54, -67.36) * mm, v(53.48, -67.5) * mm, v(53.01, -67.6) * mm, v(52.52, -67.69) * mm, v(51.89, -67.8) * mm, v(51.1, -67.9) * mm, v(50.06, -68) * mm, v(49.03, -68.04) * mm, v(48.06, -68) * mm, v(47.37, -67.94) * mm, v(46.7, -67.84) * mm, v(46.07, -67.7) * mm, v(45.47, -67.52) * mm, v(44.65, -67.27) * mm, v(43.81, -66.96) * mm, v(43, -66.64) * mm, v(42.41, -66.38) * mm, v(41.84, -66.12) * mm, v(41.28, -65.81) * mm, v(40.72, -65.47) * mm, v(40.26, -65.14) * mm, v(39.9, -64.85) * mm, v(39.56, -64.56) * mm, v(39.15, -64.18) * mm, v(38.7, -63.74) * mm, v(38.33, -63.37) * mm, v(38.05, -63.08) * mm, v(37.8, -62.81) * mm, v(37.33, -62.34) * mm, v(36.68, -61.67) * mm, v(35.85, -60.78) * mm, v(35.13, -59.94) * mm, v(34.55, -59.22) * mm, v(34.2, -58.75) * mm, v(33.93, -58.36) * mm, v(33.66, -57.97) * mm, v(33.35, -57.48) * mm, v(33.02, -56.9) * mm, v(32.72, -56.36) * mm, v(32.5, -55.94) * mm, v(32.33, -55.61) * mm, v(32.16, -55.3) * mm, v(31.95, -54.9) * mm, v(31.69, -54.38) * mm, v(31.47, -53.91) * mm, v(31.31, -53.5) * mm, v(31.2, -53.18) * mm, v(31.1, -52.85) * mm, v(30.98, -52.44) * mm, v(30.88, -51.94) * mm, v(30.79, -51.39) * mm, v(30.74, -51.06) * mm, v(30.71, -50.9) * mm]});
            skFitSpline(sketch, "E56", {"points": [v(68.4, -48.44) * mm, v(68.25, -48) * mm], "startDerivative": vector(-0.16, 0.45) * mm, "endDerivative": vector(-0.16, 0.45) * mm});
            skFitSpline(sketch, "E57.0", {"points": [v(30.73, -51) * mm, v(30.64, -50.5) * mm, v(30.5, -49.74) * mm, v(30.32, -48.78) * mm, v(30.18, -48.06) * mm, v(30.08, -47.45) * mm, v(30, -46.94) * mm, v(29.93, -46.54) * mm, v(29.86, -46.12) * mm, v(29.8, -45.7) * mm, v(29.76, -45.25) * mm, v(29.72, -44.8) * mm, v(29.7, -44.34) * mm, v(29.7, -43.92) * mm, v(29.69, -43.52) * mm, v(29.7, -43.15) * mm, v(29.7, -42.86) * mm, v(29.7, -42.64) * mm, v(29.7, -42.3) * mm, v(29.7, -41.87) * mm, v(29.72, -41.33) * mm, v(29.74, -40.9) * mm, v(29.77, -40.45) * mm, v(29.83, -39.86) * mm, v(29.93, -39.13) * mm, v(30, -38.57) * mm, v(30.05, -38.29) * mm]});
            skFitSpline(sketch, "E58", {"points": [v(31.97, -38.56) * mm, v(32, -38.31) * mm, v(32.07, -37.8) * mm, v(32.19, -37.14) * mm, v(32.3, -36.57) * mm, v(32.46, -35.98) * mm, v(32.7, -35.21) * mm, v(33.02, -34.3) * mm, v(33.35, -33.42) * mm, v(33.65, -32.6) * mm, v(33.94, -31.85) * mm, v(34.25, -31.12) * mm, v(34.58, -30.42) * mm, v(34.93, -29.73) * mm, v(35.44, -28.8) * mm, v(36.03, -27.82) * mm, v(36.73, -26.9) * mm, v(37.28, -26.25) * mm, v(37.84, -25.65) * mm, v(38.39, -25.1) * mm, v(38.93, -24.58) * mm, v(39.49, -24.08) * mm, v(40.05, -23.6) * mm, v(40.52, -23.2) * mm, v(40.91, -22.87) * mm, v(41.32, -22.52) * mm, v(41.75, -22.16) * mm, v(42.21, -21.83) * mm, v(42.7, -21.51) * mm, v(43.31, -21.19) * mm, v(44.06, -20.86) * mm, v(44.81, -20.55) * mm, v(45.62, -20.24) * mm, v(46.34, -20.02) * mm, v(46.95, -19.89) * mm, v(47.58, -19.8) * mm, v(48.36, -19.76) * mm, v(49.29, -19.8) * mm, v(50.19, -19.87) * mm, v(51.09, -20) * mm, v(51.98, -20.22) * mm, v(52.86, -20.56) * mm, v(53.7, -21) * mm, v(54.33, -21.38) * mm, v(54.8, -21.7) * mm, v(55.13, -21.91) * mm, v(55.42, -22.1) * mm, v(55.68, -22.26) * mm, v(55.9, -22.37) * mm, v(56.06, -22.41) * mm, v(56.2, -22.43) * mm, v(56.35, -22.42) * mm, v(56.55, -22.38) * mm, v(56.88, -22.3) * mm, v(57.29, -22.16) * mm, v(57.77, -22.01) * mm, v(58.31, -21.86) * mm, v(59.05, -21.67) * mm, v(60.01, -21.43) * mm, v(60.82, -21.2) * mm, v(61.46, -20.99) * mm, v(62.1, -20.76) * mm, v(62.93, -20.45) * mm, v(63.77, -20.17) * mm, v(64.47, -19.98) * mm, v(65.19, -19.83) * mm, v(66.09, -19.72) * mm, v(67.16, -19.68) * mm, v(68.22, -19.7) * mm, v(69.26, -19.76) * mm, v(70.29, -19.86) * mm, v(71.14, -19.98) * mm, v(71.82, -20.11) * mm, v(72.33, -20.23) * mm, v(72.82, -20.35) * mm, v(73.28, -20.47) * mm, v(73.7, -20.58) * mm, v(74.07, -20.68) * mm, v(74.37, -20.74) * mm, v(74.56, -20.77) * mm, v(74.7, -20.77) * mm, v(74.79, -20.77) * mm, v(74.84, -20.77) * mm]});
            skFitSpline(sketch, "E59", {"points": [v(32.18, -36.56) * mm, v(32.21, -36.31) * mm, v(32.28, -35.8) * mm, v(32.4, -35.13) * mm, v(32.52, -34.57) * mm, v(32.67, -33.97) * mm, v(32.91, -33.21) * mm, v(33.23, -32.3) * mm, v(33.56, -31.42) * mm, v(33.86, -30.6) * mm, v(34.16, -29.84) * mm, v(34.46, -29.12) * mm, v(34.8, -28.42) * mm, v(35.14, -27.73) * mm, v(35.65, -26.8) * mm, v(36.24, -25.81) * mm, v(36.94, -24.9) * mm, v(37.5, -24.24) * mm, v(38.05, -23.65) * mm, v(38.6, -23.1) * mm, v(39.15, -22.57) * mm, v(39.7, -22.08) * mm, v(40.26, -21.6) * mm, v(40.73, -21.2) * mm, v(41.12, -20.87) * mm, v(41.53, -20.52) * mm, v(41.96, -20.16) * mm, v(42.43, -19.83) * mm, v(42.9, -19.51) * mm, v(43.53, -19.18) * mm, v(44.28, -18.86) * mm, v(45.03, -18.55) * mm, v(45.83, -18.23) * mm, v(46.55, -18.01) * mm, v(47.17, -17.88) * mm, v(47.79, -17.8) * mm, v(48.57, -17.76) * mm, v(49.5, -17.8) * mm, v(50.4, -17.87) * mm, v(51.3, -18) * mm, v(52.2, -18.21) * mm, v(53.08, -18.55) * mm, v(53.9, -18.99) * mm, v(54.54, -19.38) * mm, v(55.01, -19.7) * mm, v(55.34, -19.91) * mm, v(55.63, -20.1) * mm, v(55.9, -20.26) * mm, v(56.12, -20.36) * mm, v(56.27, -20.41) * mm, v(56.4, -20.43) * mm, v(56.56, -20.42) * mm, v(56.76, -20.38) * mm, v(57.1, -20.3) * mm, v(57.5, -20.16) * mm, v(57.98, -20.01) * mm, v(58.52, -19.86) * mm, v(59.27, -19.67) * mm, v(60.22, -19.43) * mm, v(61.04, -19.2) * mm, v(61.68, -18.99) * mm, v(62.32, -18.75) * mm, v(63.14, -18.45) * mm, v(63.99, -18.17) * mm, v(64.68, -17.98) * mm, v(65.4, -17.83) * mm, v(66.3, -17.72) * mm, v(67.37, -17.68) * mm, v(68.43, -17.7) * mm, v(69.47, -17.76) * mm, v(70.5, -17.86) * mm, v(71.35, -17.98) * mm, v(72.03, -18.11) * mm, v(72.54, -18.22) * mm, v(73.03, -18.35) * mm, v(73.5, -18.47) * mm, v(73.92, -18.58) * mm, v(74.28, -18.68) * mm, v(74.58, -18.74) * mm, v(74.77, -18.77) * mm, v(74.9, -18.77) * mm, v(75, -18.77) * mm, v(75.06, -18.76) * mm]});
            skFitSpline(sketch, "E60", {"points": [v(75.06, -18.77) * mm, v(76.14, -19.18) * mm], "startDerivative": vector(1.09, -0.41) * mm, "endDerivative": vector(1.09, -0.41) * mm});
            skLineSegment(sketch, "E61", {"start": v(56.4, -20.42) * mm, "end": v(56.38, -20.42) * mm});
            skFitSpline(sketch, "E62", {"points": [v(56.4, -20.42) * mm, v(55.59, -19.89) * mm, v(54.24, -19.09) * mm, v(50.85, -18) * mm, v(47.62, -17.86) * mm, v(43.74, -18.9) * mm, v(40.45, -20.73) * mm, v(35.88, -24.92) * mm, v(32.29, -30.79) * mm, v(30.6, -35.47) * mm, v(30.05, -38.29) * mm], "startDerivative": vector(-15.58, 8.99) * mm, "endDerivative": vector(-5.7, -29.48) * mm});
            skLineSegment(sketch, "E63", {"start": v(67.8, -37.82) * mm, "end": v(67.8, -37.83) * mm});
            skLineSegment(sketch, "E64.right", {"start": v(40.24, -23.45) * mm, "end": v(40.24, -27.08) * mm});
            skLineSegment(sketch, "E65.trimOffspring", {"start": v(40.24, -32.02) * mm, "end": v(40.24, -39.1) * mm});
            skLineSegment(sketch, "E66.trimOffspring", {"start": v(57.59, -42) * mm, "end": v(57.59, -45.27) * mm});
            skLineSegment(sketch, "E67.trimOffspring", {"start": v(40.24, -58.98) * mm, "end": v(40.24, -61.74) * mm});
            skLineSegment(sketch, "E68.trimOffspring", {"start": v(57.59, -51.36) * mm, "end": v(57.59, -64.79) * mm});
            skLineSegment(sketch, "E69.trimOffspring", {"start": v(40.24, -39.9) * mm, "end": v(40.24, -47.62) * mm});
            skLineSegment(sketch, "E70", {"start": v(40.24, -48.34) * mm, "end": v(40.24, -54.98) * mm});
            skLineSegment(sketch, "E71", {"start": v(57.59, -35.53) * mm, "end": v(57.59, -22.66) * mm});
            skSolve(sketch);
        }
        {
            var Q0;
            {var subQ1=sQuery(id+"F0.wireOp",EDGE,"E2");Q0=makeQuery(id+"F0.imprint","IMPRINT",FACE,{"disambiguationData":[TD([[makeQuery(id+"F0.imprint","IMPRINT",EDGE,{"derivedFrom":subQ1}),-1.0]])]});}
            var Q1;
            {var subQ0=sQuery(id+"F0.wireOp",EDGE,"E5");Q1=makeQuery(id+"F0.imprint","IMPRINT",FACE,{"disambiguationData":[TD([[makeQuery(id+"F0.imprint","IMPRINT",EDGE,{"derivedFrom":subQ0}),1.0]])]});}
            var Q2;
            {var subQ0=sQuery(id+"F0.wireOp",EDGE,"E4");Q2=makeQuery(id+"F0.imprint","IMPRINT",FACE,{"disambiguationData":[TD([[makeQuery(id+"F0.imprint","IMPRINT",EDGE,{"derivedFrom":subQ0}),1.0]])]});}
            var Q3;
            Q3=makeQuery(id+"F0.imprint","IMPRINT",FACE,{"disambiguationData":[TD([[makeQuery(id+"F0.imprint","IMPRINT",EDGE,{"derivedFrom":sQuery(id+"F0.wireOp",EDGE,"E8")}),1.0]])]});
            var Q4;
            {var subQ2=sQuery(id+"F0.wireOp",EDGE,"E19");Q4=makeQuery(id+"F0.imprint","IMPRINT",FACE,{"disambiguationData":[TD([[makeQuery(id+"F0.imprint","IMPRINT",EDGE,{"derivedFrom":subQ2}),-1.0]])]});}
            var Q5;
            {var subQ5=sQuery(id+"F0.wireOp",EDGE,"E19");Q5=makeQuery(id+"F0.imprint","IMPRINT",FACE,{"disambiguationData":[TD([[makeQuery(id+"F0.imprint","IMPRINT",EDGE,{"derivedFrom":subQ5}),-1.0]])]});}
            extrude(context, id + "F1", {"entities" : qUnion([Q0, Q1, Q2, Q3, Q4, Q5]), "depth" : 22 * mm, "offsetDistance" : 25 * mm});
        }
        {
            var Q0;
            Q0=makeQuery(id+"F0.imprint","IMPRINT",FACE,{"disambiguationData":[TD([[makeQuery(id+"F0.imprint","IMPRINT",EDGE,{"derivedFrom":sQuery(id+"F0.wireOp",EDGE,"E19")}),-1.0]])]});
            extrude(context, id + "F2", {"entities" : qUnion([Q0]), "depth" : 25 * mm, "offsetDistance" : 25 * mm});
        }
        {
            var Q0;
            Q0=makeQuery(id+"F0.imprint","IMPRINT",FACE,{"disambiguationData":[TD([[makeQuery(id+"F0.imprint","IMPRINT",EDGE,{"derivedFrom":sQuery(id+"F0.wireOp",EDGE,"E19")}),1.0]])]});
            var Q1;
            {var subQ3=sQuery(id+"F0.wireOp",EDGE,"E71");Q1=makeQuery(id+"F0.imprint","IMPRINT",FACE,{"disambiguationData":[TD([[makeQuery(id+"F0.imprint","IMPRINT",EDGE,{"derivedFrom":subQ3}),1.0]])]});}
            var Q2;
            {var subQ3=sQuery(id+"F0.wireOp",EDGE,"E10");Q2=makeQuery(id+"F0.imprint","IMPRINT",FACE,{"disambiguationData":[TD([[makeQuery(id+"F0.imprint","IMPRINT",EDGE,{"derivedFrom":subQ3}),-1.0]])]});}
            var Q3;
            {var subQ2=sQuery(id+"F0.wireOp",EDGE,"E67.trimOffspring");Q3=makeQuery(id+"F0.imprint","IMPRINT",FACE,{"disambiguationData":[TD([[makeQuery(id+"F0.imprint","IMPRINT",EDGE,{"derivedFrom":subQ2}),1.0]])]});}
            extrude(context, id + "F3", {"entities" : qUnion([Q0, Q1, Q2, Q3]), "operationType" : NewBodyOperationType.ADD, "depth" : 2 * mm, "offsetDistance" : 25 * mm});
        }
        {
            var Q0;
            Q0=qCreatedBy(makeId("Top.planeOp"),FACE);
            cPlane(context, id + "F4", {"entities" : qUnion([Q0]), "cplaneType" : CPlaneType.OFFSET, "offset" : 5 * mm, "width" : 150 * mm, "height" : 150 * mm});
        }
    });
